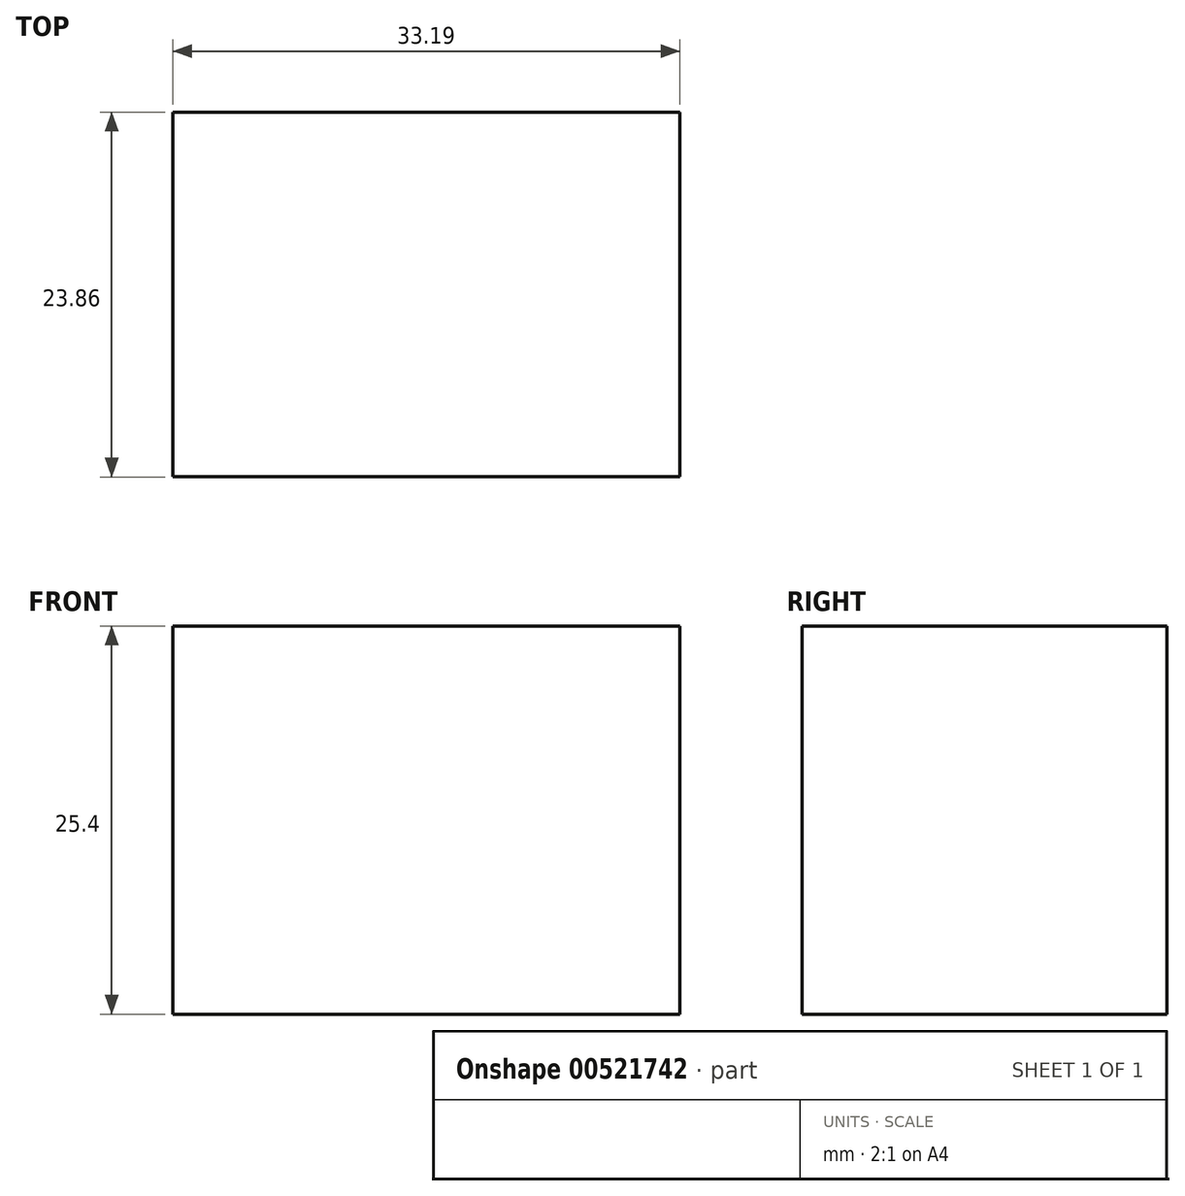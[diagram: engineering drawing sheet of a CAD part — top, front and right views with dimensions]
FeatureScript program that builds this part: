
annotation { "Feature Type Name" : "Feature", "Feature Type Description" : "" }
export const myFeature = defineFeature(function(context is Context, id is Id, definition is map)
    precondition{}
    {
        {
            var Q0;
            Q0=qCreatedBy(makeId("Top.planeOp"),FACE);
            var sketch = newSketch(context, id + "F0", { "sketchPlane" : qUnion([Q0])});
            skLineSegment(sketch, "E0.bottom", {"start": v(33.2, -23.86) * mm, "end": v(0, -23.86) * mm});
            skLineSegment(sketch, "E0.top", {"start": v(33.2, 0) * mm, "end": v(0, 0) * mm});
            skLineSegment(sketch, "E0.left", {"start": v(33.2, -23.86) * mm, "end": v(33.2, 0) * mm});
            skLineSegment(sketch, "E0.right", {"start": v(0, -23.86) * mm, "end": v(0, 0) * mm});
            skSolve(sketch);
        }
        {
            var Q0;
            Q0=makeQuery(id+"F0.imprint","IMPRINT",FACE,{"disambiguationData":[TD([[makeQuery(id+"F0.imprint","IMPRINT",EDGE,{"derivedFrom":sQuery(id+"F0.wireOp",EDGE,"E0.bottom")}),-1.0]])]});
            extrude(context, id + "F1", {"entities" : qUnion([Q0]), "oppositeDirection" : true, "depth" : 25.4 * mm, "offsetDistance" : 25.4 * mm});
        }
    });
